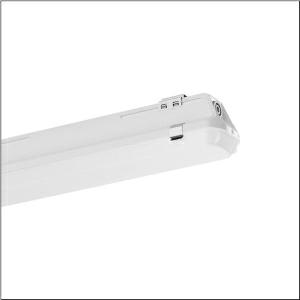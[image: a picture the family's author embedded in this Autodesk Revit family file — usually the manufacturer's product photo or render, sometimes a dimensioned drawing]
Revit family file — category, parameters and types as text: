
# Revit family: monsun_r__11_51fp107p460h_50c3
name_source: partatom
category: Lighting Fixtures
units: mm (PartAtom-declared; Revit-internal decimal feet)

## family parameters
Cut with Voids When Loaded = No
Host = Face
Light Source = No
Part Type = Normal
Room Calculation Point = No
Round Connector Dimension = Use Diameter
Shared = No

## types (1)
- Monsun® 11 (1 x LED, 5800 lm, 32.5 W, 4000K)
    Apparent Load = 33 VA
    CIE Flux Codes = 47 77 93 94 100
    Color Rendering = 80
    Color Temperature = 4000K
    Default Elevation = 1800 mm
    Description = Monsun® 11, damp-proof luminaire, chain hanger, primary optical cover: enclosure, of PMMA, light emission: direct distribution, primary light characteristic: symmetric, installation type: suspended mounting, surface-mounted, horizontal mounting, vertical mounting, LED, rated luminous flux: 5.800lm, luminous efficacy: 178lm/W, light colour: 840, colour temperature: 4000K, control gear: ECG, with terminal, 3-pole, max. 2.5mm², mains connection: 220..240V, AC, 50/60Hz, rated input power: 33W, luminaire housing, of glass-fibre reinforced polyester, uncoated, bright grey, incl. chain hanger, length: 1.590mm, width: 90mm, height: 88mm, clip for enclosure, of stainless steel (V2A), ceiling mounting element, of stainless steel (V2A), chain hanger, of stainless steel (V2A), protection rating (complete): IP66, insulation class (complete): insulation class I (protective earthing), certification: CE, ENEC, VDE, UKCA, protection symbol: D, impact resistance: IK04, permissible operating ambient temperature: -35..+40°C, standard: EN 50419, EN 60598-2-1, no direct snow, no direct sun, no direct rain, for indoor or canopied outdoor use, corresponds to IFS (International Featured Standards) requirements for safety and quality in the food industry, contact your sales advisor before using the luminaires in applications with unclear chemical exposure, large temperature fluctuations or condensation-forming humidity, LABS conformity tested according to VDMA 24364:2018-05, packaging unit: 1 piece
    Height = 89 mm
    Lamp = 1 x LED
    Lamp Light Flux = 5800 lm
    Lamp Power = 32.5 W
    Lamp count = 1
    Length = 1590 mm
    Luminous efficacy = 178 lm/W
    Manufacturer = Siteco
    ModVariant = No
    Model = 51FP107P460H
    Mounting Place = Ceiling
    Mounting Type = Surface mounted
    Number of Poles = 1
    OnlyDefault = Yes
    Power Factor = 1
    Product Name = Monsun® 11
    Product group = damp-proof luminaire
    ProductGroupID = 300
    Protection Class = Protection class I
    Protection Degree = IP 66
    RLX_Detail_Level = 1
    RLX_Emergency_Light_Flux = 0 lm
    RLX_Emergency_Type = 0
    RLX_Emergency_Type_DB = No
    RlxData = <blob elided: 88905 chars, md5=60b8ee86>
    Socket = socket
    Standby Power = 0 W
    System Light Flux = 5800 lm
    System Power = 33 W
    Type Comments = Product without accessories
    Type Image = l_1004748.jpg
    URL = http://relux.com
    VarID = ---
    Voltage = 0 V
    Weight = 0.00 kg
    Width = 90 mm

## geometry (parser evidence)
native form markers: Blend x4, Sweep x11
no freeform markers — native parametric forms only
